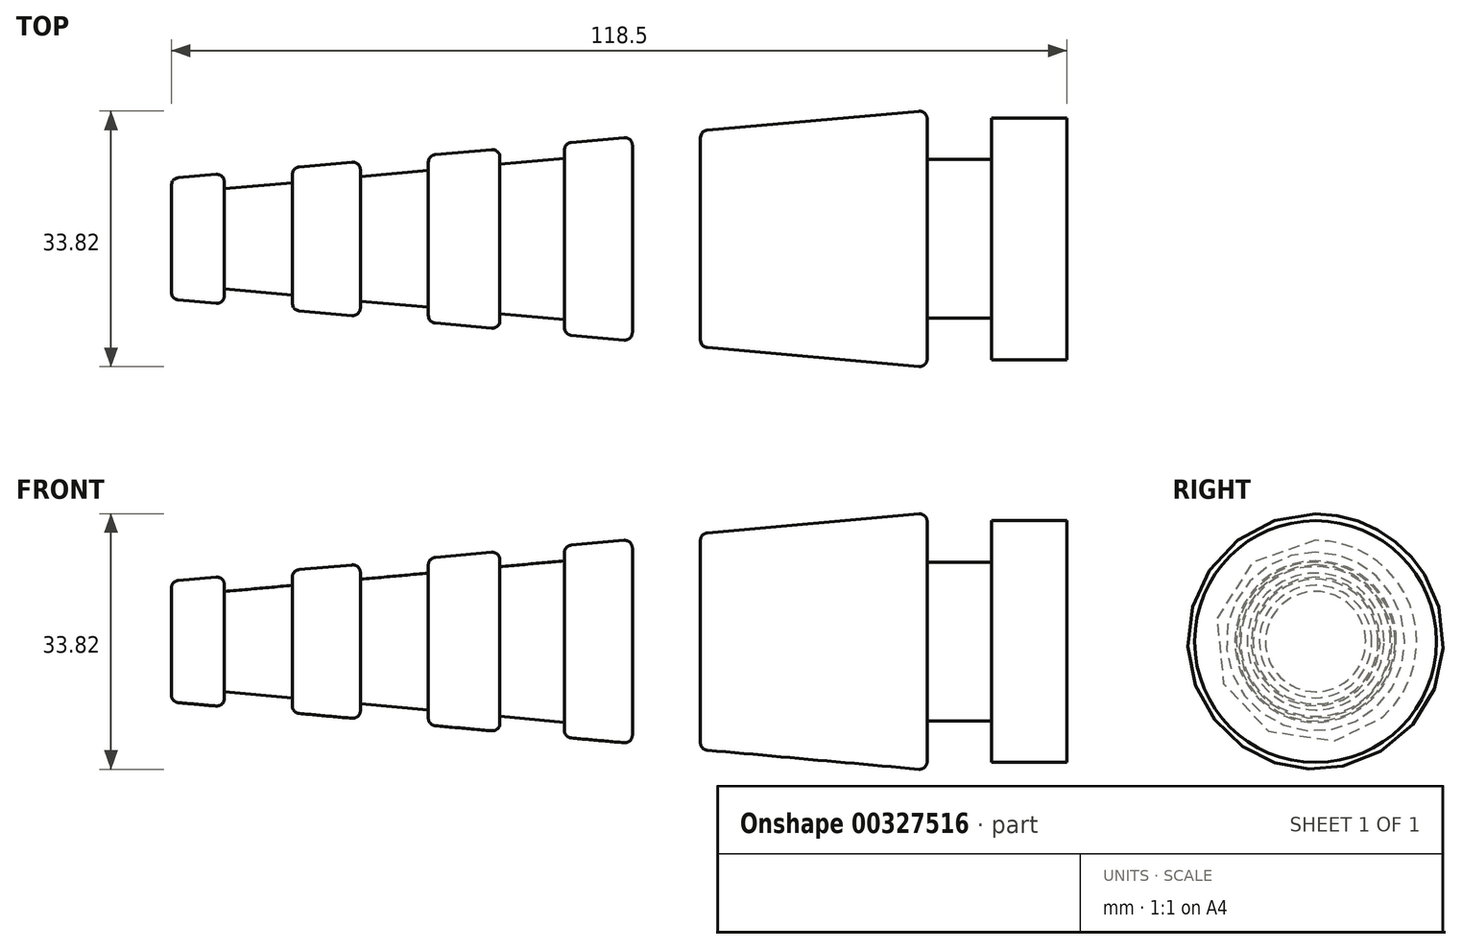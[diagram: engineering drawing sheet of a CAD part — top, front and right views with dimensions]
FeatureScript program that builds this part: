
annotation { "Feature Type Name" : "Feature", "Feature Type Description" : "" }
export const myFeature = defineFeature(function(context is Context, id is Id, definition is map)
    precondition{}
    {
        {
            var Q0;
            Q0=qCreatedBy(makeId("Front.planeOp"),FACE);
            var sketch = newSketch(context, id + "F0", { "sketchPlane" : qUnion([Q0])});
            skLineSegment(sketch, "E0.bottom", {"start": v(75.03, 0) * mm, "end": v(65.03, 0) * mm});
            skLineSegment(sketch, "E0.top", {"start": v(75.03, 16) * mm, "end": v(65.03, 16) * mm});
            skLineSegment(sketch, "E0.left", {"start": v(75.03, 0) * mm, "end": v(75.03, 16) * mm});
            skLineSegment(sketch, "E0.right", {"start": v(65.03, 0) * mm, "end": v(65.03, 16) * mm});
            skLineSegment(sketch, "E1", {"start": v(65.03, 0) * mm, "end": v(56.53, 0) * mm});
            skLineSegment(sketch, "E2", {"start": v(56.53, 0) * mm, "end": v(56.53, 10.5) * mm});
            skLineSegment(sketch, "E3", {"start": v(56.53, 10.5) * mm, "end": v(65.03, 10.5) * mm});
            skLineSegment(sketch, "E4", {"start": v(56.53, 0) * mm, "end": v(56.53, 17) * mm});
            skLineSegment(sketch, "E5", {"start": v(-43.47, 0) * mm, "end": v(-43.47, 8) * mm});
            skLineSegment(sketch, "E6", {"start": v(-43.47, 8) * mm, "end": v(-36.47, 8.63) * mm});
            skLineSegment(sketch, "E7", {"start": v(56.53, 0) * mm, "end": v(26.53, 0) * mm});
            skLineSegment(sketch, "E8", {"start": v(26.53, 0) * mm, "end": v(17.53, 0) * mm});
            skLineSegment(sketch, "E9", {"start": v(17.53, 0) * mm, "end": v(8.53, 0) * mm});
            skLineSegment(sketch, "E10", {"start": v(8.53, 0) * mm, "end": v(-0.47, 0) * mm});
            skLineSegment(sketch, "E11", {"start": v(-0.47, 0) * mm, "end": v(-9.47, 0) * mm});
            skLineSegment(sketch, "E12", {"start": v(-9.47, 0) * mm, "end": v(-18.47, 0) * mm});
            skLineSegment(sketch, "E13", {"start": v(-18.47, 0) * mm, "end": v(-27.47, 0) * mm});
            skLineSegment(sketch, "E14", {"start": v(-36.47, 0) * mm, "end": v(-43.47, 0) * mm});
            skLineSegment(sketch, "E15", {"start": v(-36.47, 0) * mm, "end": v(-27.47, 0) * mm});
            skLineSegment(sketch, "E16", {"start": v(-36.47, 0) * mm, "end": v(-36.47, 8.63) * mm});
            skLineSegment(sketch, "E17", {"start": v(-27.47, 0) * mm, "end": v(-27.47, 9.44) * mm});
            skLineSegment(sketch, "E18", {"start": v(-18.47, 0) * mm, "end": v(-18.47, 10.25) * mm});
            skLineSegment(sketch, "E19", {"start": v(-9.47, 0) * mm, "end": v(-9.47, 11.06) * mm});
            skLineSegment(sketch, "E20", {"start": v(0, 0) * mm, "end": v(0, 11.91) * mm});
            skLineSegment(sketch, "E21", {"start": v(8.53, 0) * mm, "end": v(8.53, 12.68) * mm});
            skLineSegment(sketch, "E22", {"start": v(17.53, 0) * mm, "end": v(17.53, 13.49) * mm});
            skLineSegment(sketch, "E23", {"start": v(26.53, 0) * mm, "end": v(26.53, 14.3) * mm});
            skLineSegment(sketch, "E24.trimOffspring", {"start": v(26.53, 14.3) * mm, "end": v(56.53, 17) * mm});
            skLineSegment(sketch, "E25.trimOffspring", {"start": v(8.53, 12.68) * mm, "end": v(17.53, 13.49) * mm});
            skLineSegment(sketch, "E26.trimOffspring", {"start": v(-9.47, 11.06) * mm, "end": v(0, 11.91) * mm});
            skLineSegment(sketch, "E27.trimOffspring", {"start": v(-27.47, 9.44) * mm, "end": v(-18.47, 10.25) * mm});
            skLineSegment(sketch, "E28", {"start": v(26.53, 0) * mm, "end": v(26.53, 12.3) * mm});
            skLineSegment(sketch, "E29", {"start": v(-43.47, 0) * mm, "end": v(-43.47, 6) * mm});
            skLineSegment(sketch, "E30", {"start": v(-36.47, 6.63) * mm, "end": v(-27.47, 7.44) * mm});
            skLineSegment(sketch, "E31.trimOffspring", {"start": v(-18.47, 8.25) * mm, "end": v(-9.47, 9.06) * mm});
            skLineSegment(sketch, "E32.trimOffspring", {"start": v(0, 9.91) * mm, "end": v(8.53, 10.68) * mm});
            skLineSegment(sketch, "E33.trimOffspring", {"start": v(17.53, 11.49) * mm, "end": v(26.53, 12.3) * mm});
            skLineSegment(sketch, "E34", {"start": v(-62, 0) * mm, "end": v(108.57, 0) * mm});
            skSolve(sketch);
        }
        {
            var Q0;
            Q0=makeQuery(id+"F0.imprint","IMPRINT",FACE,{"disambiguationData":[TD([[makeQuery(id+"F0.imprint","IMPRINT",EDGE,{"derivedFrom":sQuery(id+"F0.wireOp",EDGE,"E23")}),-1.0]])]});
            var Q1;
            {var subQ4=sQuery(id+"F0.wireOp",EDGE,"E28");Q1=makeQuery(id+"F0.imprint","IMPRINT",FACE,{"disambiguationData":[TD([[makeQuery(id+"F0.imprint","IMPRINT",EDGE,{"derivedFrom":subQ4}),1.0]])]});}
            var Q2;
            {var subQ0=sQuery(id+"F0.wireOp",EDGE,"E25.trimOffspring");Q2=makeQuery(id+"F0.imprint","IMPRINT",FACE,{"disambiguationData":[TD([[makeQuery(id+"F0.imprint","IMPRINT",EDGE,{"derivedFrom":subQ0}),-1.0]])]});}
            var Q3;
            {var subQ3=sQuery(id+"F0.wireOp",EDGE,"E32.trimOffspring");Q3=makeQuery(id+"F0.imprint","IMPRINT",FACE,{"disambiguationData":[TD([[makeQuery(id+"F0.imprint","IMPRINT",EDGE,{"derivedFrom":subQ3}),-1.0]])]});}
            var Q4;
            {var subQ0=sQuery(id+"F0.wireOp",EDGE,"E26.trimOffspring");Q4=makeQuery(id+"F0.imprint","IMPRINT",FACE,{"disambiguationData":[TD([[makeQuery(id+"F0.imprint","IMPRINT",EDGE,{"derivedFrom":subQ0}),-1.0]])]});}
            var Q5;
            {var subQ3=sQuery(id+"F0.wireOp",EDGE,"E31.trimOffspring");Q5=makeQuery(id+"F0.imprint","IMPRINT",FACE,{"disambiguationData":[TD([[makeQuery(id+"F0.imprint","IMPRINT",EDGE,{"derivedFrom":subQ3}),-1.0]])]});}
            var Q6;
            {var subQ0=sQuery(id+"F0.wireOp",EDGE,"E27.trimOffspring");Q6=makeQuery(id+"F0.imprint","IMPRINT",FACE,{"disambiguationData":[TD([[makeQuery(id+"F0.imprint","IMPRINT",EDGE,{"derivedFrom":subQ0}),-1.0]])]});}
            var Q7;
            {var subQ3=sQuery(id+"F0.wireOp",EDGE,"E30");Q7=makeQuery(id+"F0.imprint","IMPRINT",FACE,{"disambiguationData":[TD([[makeQuery(id+"F0.imprint","IMPRINT",EDGE,{"derivedFrom":subQ3}),-1.0]])]});}
            var Q8;
            Q8=makeQuery(id+"F0.imprint","IMPRINT",FACE,{"disambiguationData":[TD([[makeQuery(id+"F0.imprint","IMPRINT",EDGE,{"derivedFrom":sQuery(id+"F0.wireOp",EDGE,"E5")}),-1.0]])]});
            var Q9;
            {var subQ3=sQuery(id+"F0.wireOp",EDGE,"E3");Q9=makeQuery(id+"F0.imprint","IMPRINT",FACE,{"disambiguationData":[TD([[makeQuery(id+"F0.imprint","IMPRINT",EDGE,{"derivedFrom":subQ3}),-1.0]])]});}
            var Q10;
            {var subQ1=sQuery(id+"F0.wireOp",EDGE,"E0.top");Q10=makeQuery(id+"F0.imprint","IMPRINT",FACE,{"disambiguationData":[TD([[makeQuery(id+"F0.imprint","IMPRINT",EDGE,{"derivedFrom":subQ1}),1.0]])]});}
            var Q11;
            Q11=sQuery(id+"F0.wireOp",EDGE,"E34");
            revolve(context, id + "F1", {"entities" : qUnion([Q0, Q1, Q2, Q3, Q4, Q5, Q6, Q7, Q8, Q9, Q10]), "axis" : qUnion([Q11]), "revolveType" : RevolveType.FULL});
        }
        {
            var Q0;
            Q0=makeQuery(id+"F1.opRevolve","SWEPT_EDGE",EDGE,{"disambiguationData":[OSD([sQuery(id+"F0.wireOp",EDGE,"E4"),sQuery(id+"F0.wireOp",EDGE,"E24.trimOffspring")])]});
            var Q1;
            Q1=makeQuery(id+"F1.opRevolve","SWEPT_EDGE",EDGE,{"disambiguationData":[OSD([sQuery(id+"F0.wireOp",EDGE,"E23"),sQuery(id+"F0.wireOp",EDGE,"E24.trimOffspring")])]});
            var Q2;
            Q2=makeQuery(id+"F1.opRevolve","SWEPT_EDGE",EDGE,{"disambiguationData":[OSD([sQuery(id+"F0.wireOp",EDGE,"E22"),sQuery(id+"F0.wireOp",EDGE,"E25.trimOffspring")])]});
            var Q3;
            Q3=makeQuery(id+"F1.opRevolve","SWEPT_EDGE",EDGE,{"disambiguationData":[OSD([sQuery(id+"F0.wireOp",EDGE,"E21"),sQuery(id+"F0.wireOp",EDGE,"E25.trimOffspring")])]});
            var Q4;
            Q4=makeQuery(id+"F1.opRevolve","SWEPT_EDGE",EDGE,{"disambiguationData":[OSD([sQuery(id+"F0.wireOp",EDGE,"E20"),sQuery(id+"F0.wireOp",EDGE,"E26.trimOffspring")])]});
            var Q5;
            Q5=makeQuery(id+"F1.opRevolve","SWEPT_EDGE",EDGE,{"disambiguationData":[OSD([sQuery(id+"F0.wireOp",EDGE,"E19"),sQuery(id+"F0.wireOp",EDGE,"E26.trimOffspring")])]});
            var Q6;
            Q6=makeQuery(id+"F1.opRevolve","SWEPT_EDGE",EDGE,{"disambiguationData":[OSD([sQuery(id+"F0.wireOp",EDGE,"E18"),sQuery(id+"F0.wireOp",EDGE,"E27.trimOffspring")])]});
            var Q7;
            Q7=makeQuery(id+"F1.opRevolve","SWEPT_EDGE",EDGE,{"disambiguationData":[OSD([sQuery(id+"F0.wireOp",EDGE,"E17"),sQuery(id+"F0.wireOp",EDGE,"E27.trimOffspring")])]});
            var Q8;
            Q8=makeQuery(id+"F1.opRevolve","SWEPT_EDGE",EDGE,{"disambiguationData":[OSD([sQuery(id+"F0.wireOp",EDGE,"E5"),sQuery(id+"F0.wireOp",EDGE,"E6")])]});
            var Q9;
            Q9=makeQuery(id+"F1.opRevolve","SWEPT_EDGE",EDGE,{"disambiguationData":[OSD([sQuery(id+"F0.wireOp",EDGE,"E6"),sQuery(id+"F0.wireOp",EDGE,"E16")])]});
            fillet(context, id + "F2", {"entities" : qUnion([Q0, Q1, Q2, Q3, Q4, Q5, Q6, Q7, Q8, Q9]), "radius" : 1 * mm, "tangentPropagation" : true, "allowEdgeOverflow" : false});
        }
    });
